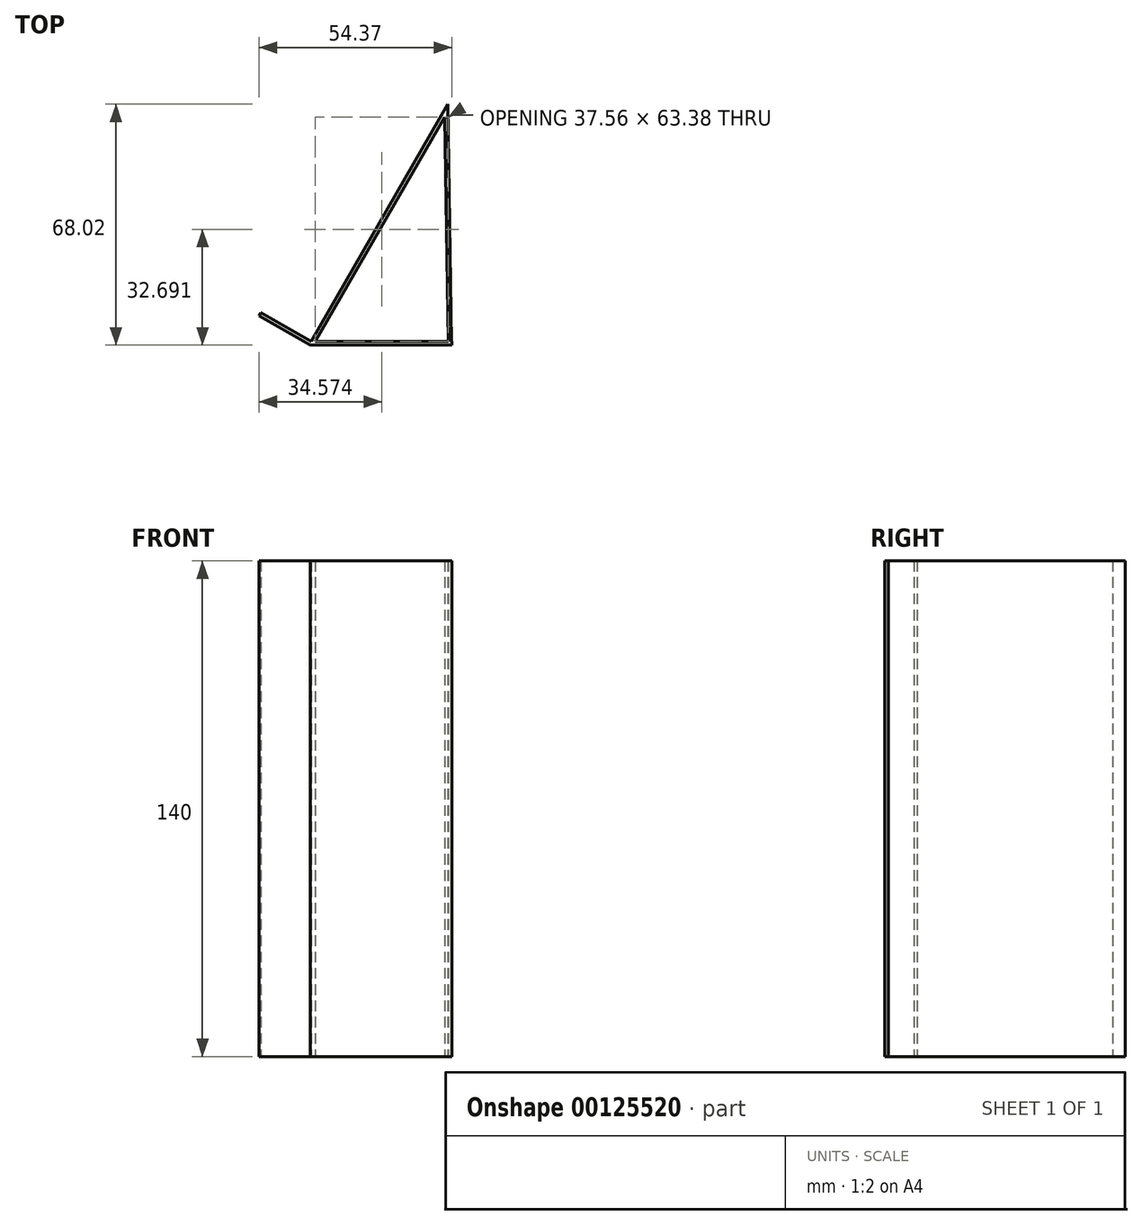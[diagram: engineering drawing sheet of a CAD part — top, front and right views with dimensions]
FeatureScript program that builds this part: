
annotation { "Feature Type Name" : "Feature", "Feature Type Description" : "" }
export const myFeature = defineFeature(function(context is Context, id is Id, definition is map)
    precondition{}
    {
        {
            var Q0;
            Q0=qCreatedBy(makeId("Top.planeOp"),FACE);
            var sketch = newSketch(context, id + "F0", { "sketchPlane" : qUnion([Q0])});
            skLineSegment(sketch, "E0.bottom", {"start": v(0, 0) * mm, "end": v(-40, 0) * mm});
            skLineSegment(sketch, "E0.top", {"start": v(0, 1) * mm, "end": v(-0.02, 1) * mm});
            skLineSegment(sketch, "E0.left", {"start": v(0, 0) * mm, "end": v(0, 1) * mm});
            skLineSegment(sketch, "E1", {"start": v(-40, 0) * mm, "end": v(-54.37, 8.3) * mm});
            skLineSegment(sketch, "E2", {"start": v(-54.37, 8.3) * mm, "end": v(-53.87, 9.16) * mm});
            skLineSegment(sketch, "E3", {"start": v(-53.87, 9.16) * mm, "end": v(-39.73, 1) * mm});
            skLineSegment(sketch, "E4", {"start": v(0, 0) * mm, "end": v(-1.04, 68.02) * mm});
            skLineSegment(sketch, "E5", {"start": v(-1.1, 72) * mm, "end": v(-2.1, 71.98) * mm});
            skLineSegment(sketch, "E6", {"start": v(-1.98, 64.38) * mm, "end": v(-1.02, 1) * mm});
            skLineSegment(sketch, "E7.trimOffspring", {"start": v(-1.02, 1) * mm, "end": v(-38.58, 1) * mm});
            skLineSegment(sketch, "E8", {"start": v(-39.73, 1) * mm, "end": v(-1.04, 68.02) * mm});
            skLineSegment(sketch, "E9", {"start": v(12.67, 91.76) * mm, "end": v(13.54, 91.26) * mm});
            skLineSegment(sketch, "E10", {"start": v(-1.98, 64.38) * mm, "end": v(-38.58, 1) * mm});
            skLineSegment(sketch, "E11", {"start": v(-38.58, 1) * mm, "end": v(-39.15, 0) * mm});
            skSolve(sketch);
        }
        {
            var Q0;
            Q0=qSketchRegion(id+"F0",true);
            extrude(context, id + "F1", {"entities" : qUnion([Q0]), "depth" : 140 * mm});
        }
    });
